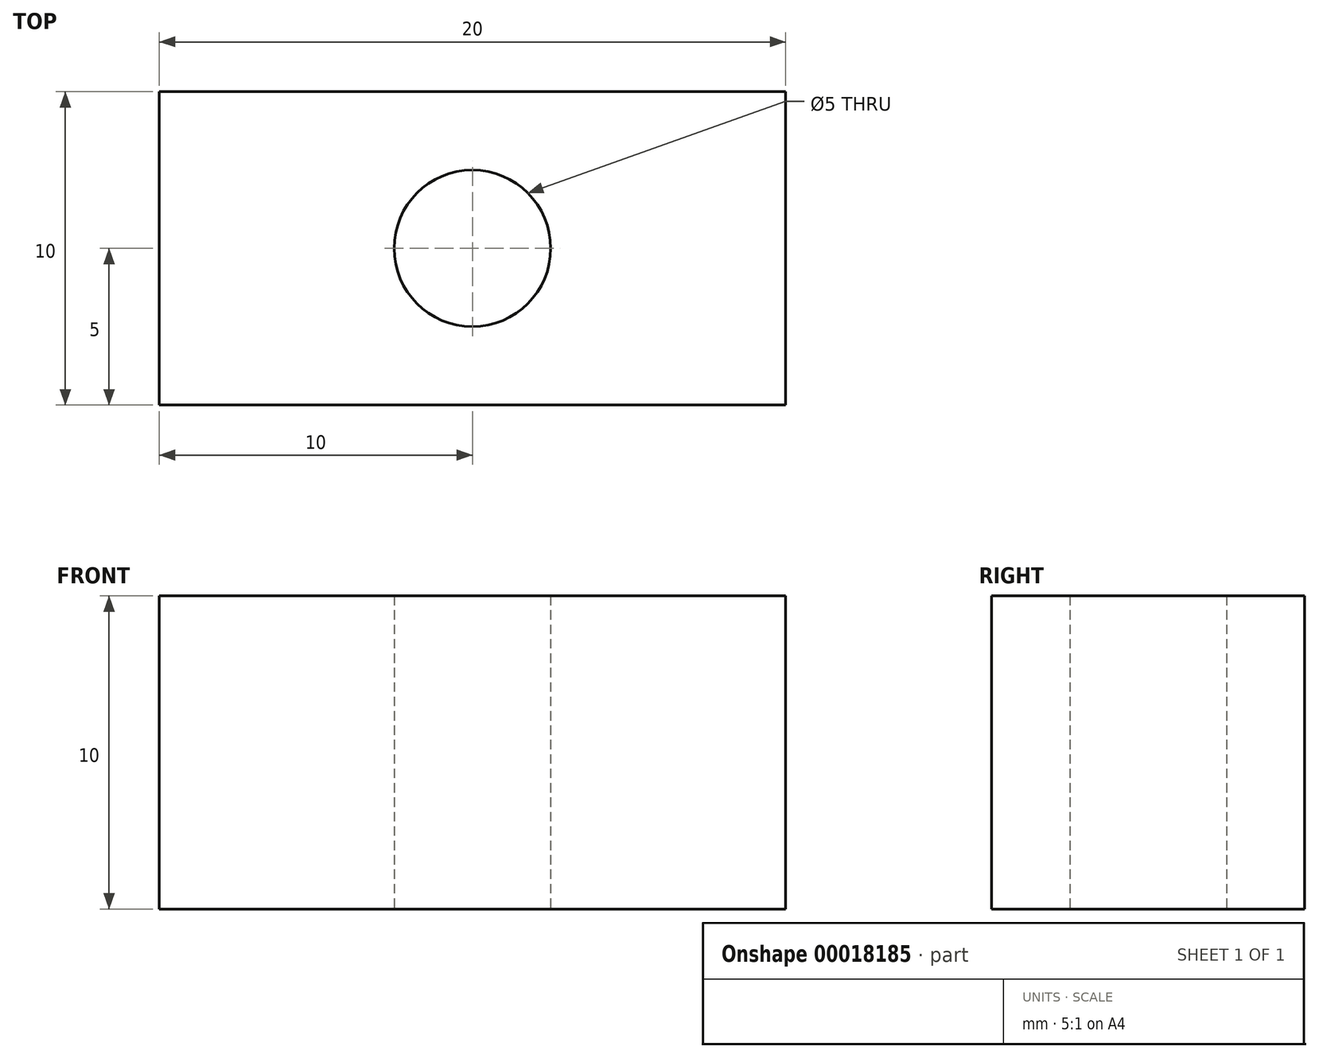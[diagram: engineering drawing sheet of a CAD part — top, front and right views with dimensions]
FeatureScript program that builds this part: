
annotation { "Feature Type Name" : "Feature", "Feature Type Description" : "" }
export const myFeature = defineFeature(function(context is Context, id is Id, definition is map)
    precondition{}
    {
        {
            var Q0;
            Q0=qCreatedBy(makeId("Top.planeOp"),FACE);
            var sketch = newSketch(context, id + "F0", { "sketchPlane" : qUnion([Q0])});
            skLineSegment(sketch, "E0.bottom", {"start": v(0, 0) * mm, "end": v(-20, 0) * mm});
            skLineSegment(sketch, "E0.top", {"start": v(0, -10) * mm, "end": v(-20, -10) * mm});
            skLineSegment(sketch, "E0.left", {"start": v(0, 0) * mm, "end": v(0, -10) * mm});
            skLineSegment(sketch, "E0.right", {"start": v(-20, 0) * mm, "end": v(-20, -10) * mm});
            skCircle(sketch, "E1", {"center": v(-10, -5) * mm, "radius": 2.5 * mm});
            skLineSegment(sketch, "E2", {"start": v(-20.87, -5) * mm, "end": v(3.54, -5) * mm, "construction": true});
            skLineSegment(sketch, "E3", {"start": v(-10, 1.26) * mm, "end": v(-10, -11.5) * mm, "construction": true});
            skSolve(sketch);
        }
        {
            var Q0;
            Q0=makeQuery(id+"F0.imprint","IMPRINT",FACE,{"disambiguationData":[TD([[makeQuery(id+"F0.imprint","IMPRINT",EDGE,{"derivedFrom":sQuery(id+"F0.wireOp",EDGE,"E0.bottom")}),1.0]])]});
            extrude(context, id + "F1", {"entities" : qUnion([Q0]), "depth" : 10 * mm});
        }
    });
